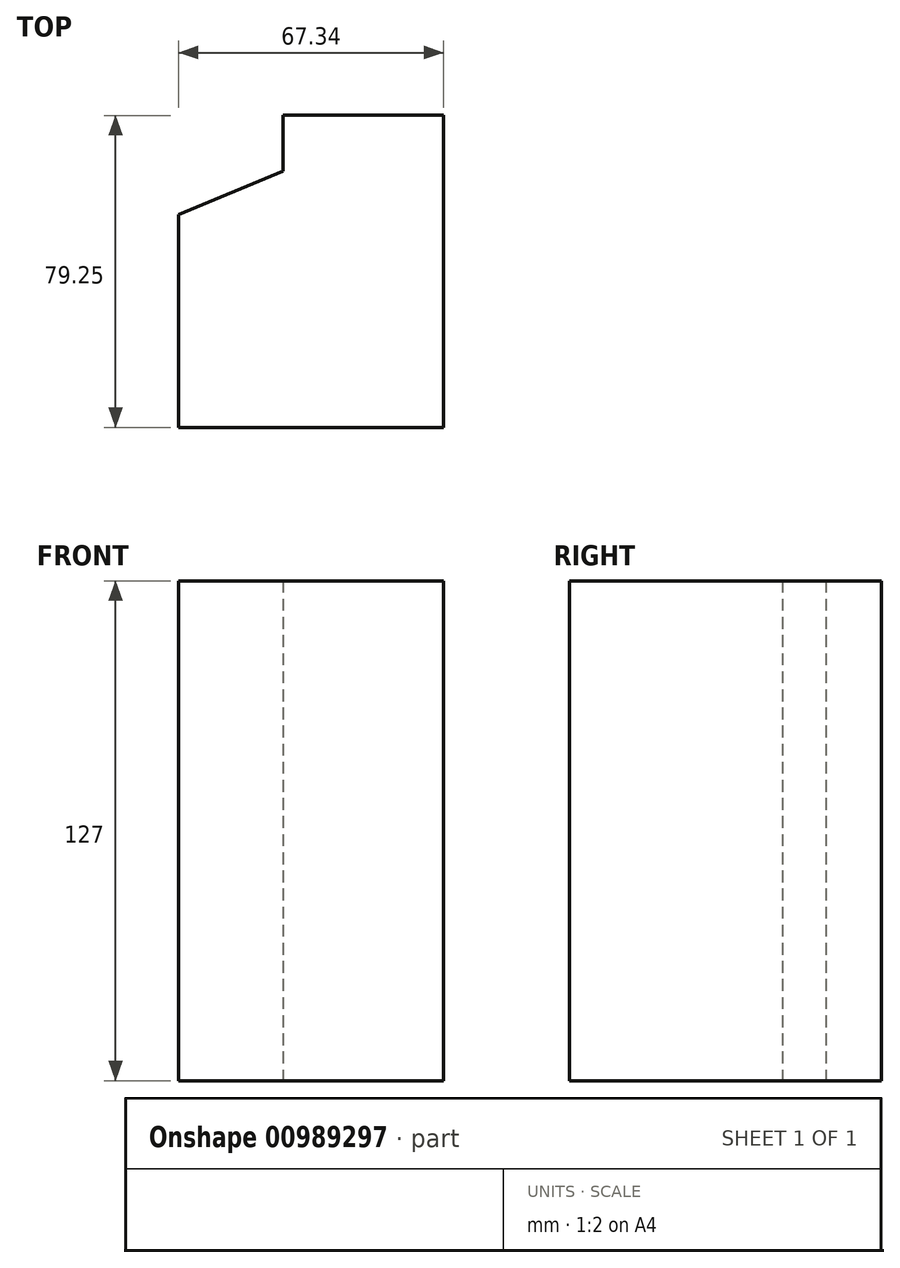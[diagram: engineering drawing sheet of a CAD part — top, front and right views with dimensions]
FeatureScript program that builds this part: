
annotation { "Feature Type Name" : "Feature", "Feature Type Description" : "" }
export const myFeature = defineFeature(function(context is Context, id is Id, definition is map)
    precondition{}
    {
        {
            var Q0;
            Q0=qCreatedBy(makeId("Top.planeOp"),FACE);
            var sketch = newSketch(context, id + "F0", { "sketchPlane" : qUnion([Q0])});
            skLineSegment(sketch, "E0.bottom", {"start": v(10.2, -18.67) * mm, "end": v(-57.15, -18.67) * mm});
            skLineSegment(sketch, "E0.top", {"start": v(10.2, 35.39) * mm, "end": v(-57.15, 35.39) * mm});
            skLineSegment(sketch, "E0.left", {"start": v(10.2, -18.67) * mm, "end": v(10.2, 35.39) * mm});
            skLineSegment(sketch, "E0.right", {"start": v(-57.15, -18.67) * mm, "end": v(-57.15, 35.39) * mm});
            skPoint(sketch, "E0.middle", {"position": v(-23.48, 8.36) * mm});
            skLineSegment(sketch, "E1.bottom", {"start": v(10.2, 46.38) * mm, "end": v(-30.58, 46.38) * mm});
            skLineSegment(sketch, "E1.top", {"start": v(10.2, 60.58) * mm, "end": v(-30.58, 60.58) * mm});
            skLineSegment(sketch, "E1.left", {"start": v(10.2, 46.38) * mm, "end": v(10.2, 60.58) * mm});
            skLineSegment(sketch, "E1.right", {"start": v(-30.58, 46.38) * mm, "end": v(-30.58, 60.58) * mm});
            skPoint(sketch, "E1.middle", {"position": v(-10.2, 53.48) * mm});
            skLineSegment(sketch, "E2", {"start": v(-57.15, 35.39) * mm, "end": v(-30.58, 46.38) * mm});
            skLineSegment(sketch, "E3", {"start": v(10.2, 46.38) * mm, "end": v(10.2, 35.39) * mm});
            skSolve(sketch);
        }
        {
            var Q0;
            Q0 = qSketchRegion(id + "F0", true);
            extrude(context, id + "F1", {"entities" : qUnion([Q0]), "endBound" : BoundingType.SYMMETRIC, "depth" : 127 * mm, "offsetDistance" : 25.4 * mm});
        }
    });
